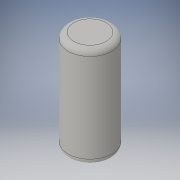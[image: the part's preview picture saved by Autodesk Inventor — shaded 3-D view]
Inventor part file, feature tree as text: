
AUTODESK INVENTOR PART (.ipt)
format: ipt  version: 2016 (Build 200138000, 138)  size: 125,440 bytes
history: native  units: in
note: dims shown in document units (in); Inventor stores cm internally (conversion verified against a paired STEP export)
features: fillet x3, extrude x1, sketch x1
ambient origin geometry x8: Origin, YZ Plane, XZ Plane, XY Plane, X Axis, Y Axis, Z Axis, Center Point
bodies: Solid1 (feature_tree)
feature tree (5):
  extrude  "Extrusion1"  Depth=1.1in
  fillet  "Fillet1"  Radius=0.48in
  fillet  "Fillet2"  [1 undecoded]
  fillet  "Fillet3"  Radius=0.24in
  sketch  "Sketch1"  dims[d1=0.24in d2=1.1in d3=0.48in d4=0.0in d5=0.24in d6=0.0625in d7=0.0625in]
note: 1 required parameter value undecoded (feature->parameter linkage not recoverable at this tier; creation-order binding heuristic only, values carry confidence <= 0.55)
